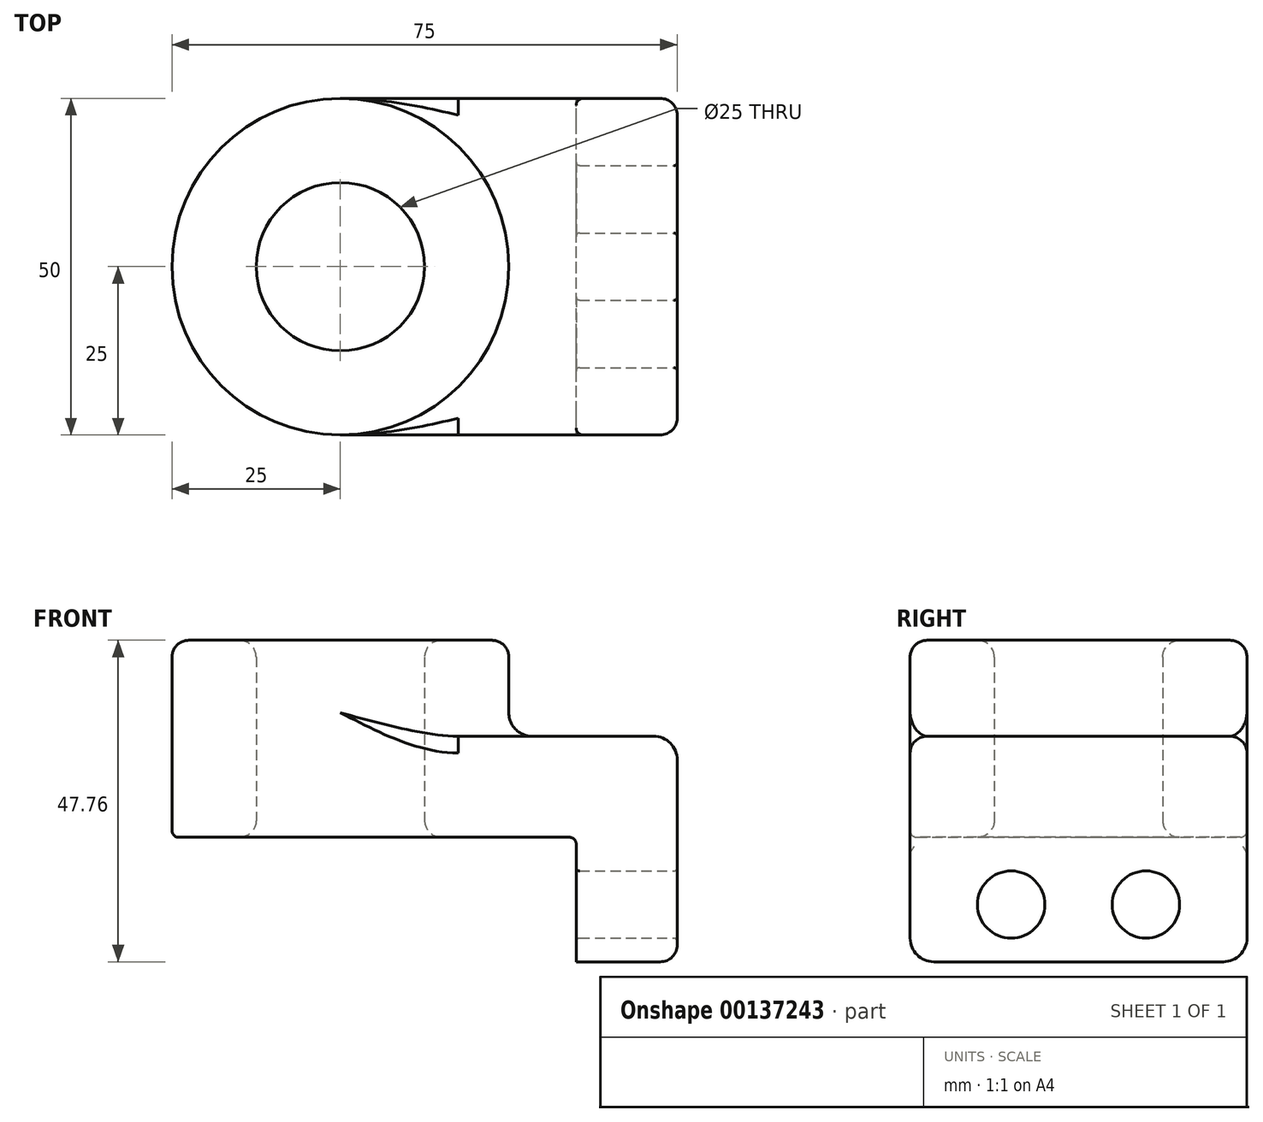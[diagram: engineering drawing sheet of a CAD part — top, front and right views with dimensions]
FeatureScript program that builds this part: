
annotation { "Feature Type Name" : "Feature", "Feature Type Description" : "" }
export const myFeature = defineFeature(function(context is Context, id is Id, definition is map)
    precondition{}
    {
        {
            var Q0;
            Q0=qCreatedBy(makeId("Top.planeOp"),FACE);
            var sketch = newSketch(context, id + "F0", { "sketchPlane" : qUnion([Q0])});
            skLineSegment(sketch, "E0.bottom", {"start": v(25, 25) * mm, "end": v(-25, 25) * mm});
            skLineSegment(sketch, "E0.top", {"start": v(25, -25) * mm, "end": v(-25, -25) * mm});
            skLineSegment(sketch, "E0.left", {"start": v(25, 25) * mm, "end": v(25, -25) * mm});
            skLineSegment(sketch, "E0.right", {"start": v(-25, 25) * mm, "end": v(-25, -25) * mm});
            skPoint(sketch, "E0.middle", {"position": v(0, 0) * mm});
            skCircle(sketch, "E1", {"center": v(-25, 0) * mm, "radius": 25 * mm});
            skCircle(sketch, "E2", {"center": v(-25, 0) * mm, "radius": 12.5 * mm});
            skSolve(sketch);
        }
        {
            var Q0;
            Q0 = qSketchRegion(id + "F0", true);
            extrude(context, id + "F1", {"entities" : qUnion([Q0]), "depth" : 15 * mm});
        }
        {
            var Q0;
            {var subQ1=sQuery(id+"F0.wireOp",EDGE,"E0.right");var subQ3=sQuery(id+"F0.wireOp",EDGE,"E2");var subQ4=makeQuery(id+"F0.imprint","INTERSECT",VERTEX,{"disambiguationData":[OD(0.0)],"derivedFrom":[subQ1,subQ3]});Q0=makeQuery(id+"F0.imprint","IMPRINT",FACE,{"disambiguationData":[TD([[makeQuery(id+"F0.imprint","IMPRINT",EDGE,{"disambiguationData":[TD([[subQ4,-1.0]])],"derivedFrom":subQ3}),-1.0]])]});}
            var Q1;
            {var subQ1=sQuery(id+"F0.wireOp",EDGE,"E0.right");var subQ3=sQuery(id+"F0.wireOp",EDGE,"E2");var subQ4=makeQuery(id+"F0.imprint","INTERSECT",VERTEX,{"disambiguationData":[OD(0.0)],"derivedFrom":[subQ1,subQ3]});Q1=makeQuery(id+"F0.imprint","IMPRINT",FACE,{"disambiguationData":[TD([[makeQuery(id+"F0.imprint","IMPRINT",EDGE,{"disambiguationData":[TD([[subQ4,1.0]])],"derivedFrom":subQ3}),-1.0]])]});}
            extrude(context, id + "F2", {"entities" : qUnion([Q0, Q1]), "operationType" : NewBodyOperationType.ADD, "depth" : 29.26 * mm});
        }
        {
            var Q0;
            Q0=makeQuery(id+"F1.opExtrude","SWEPT_FACE",FACE,{"disambiguationData":[OSD([sQuery(id+"F0.wireOp",EDGE,"E0.left")])]});
            var sketch = newSketch(context, id + "F3", { "sketchPlane" : qUnion([Q0])});
            skLineSegment(sketch, "E3.bottom", {"start": v(-25, 15) * mm, "end": v(25, 15) * mm});
            skLineSegment(sketch, "E3.top", {"start": v(-25, -18.5) * mm, "end": v(25, -18.5) * mm});
            skLineSegment(sketch, "E3.left", {"start": v(-25, 15) * mm, "end": v(-25, -18.5) * mm});
            skLineSegment(sketch, "E3.right", {"start": v(25, 15) * mm, "end": v(25, -18.5) * mm});
            skCircle(sketch, "E4", {"center": v(-10, -10) * mm, "radius": 5 * mm});
            skLineSegment(sketch, "E5", {"start": v(0, 0) * mm, "end": v(0, -18.5) * mm, "construction": true});
            skCircle(sketch, "E6.MirrorC", {"center": v(10, -10) * mm, "radius": 5 * mm});
            skSolve(sketch);
        }
        {
            var Q0;
            Q0 = qSketchRegion(id + "F3", true);
            extrude(context, id + "F4", {"entities" : qUnion([Q0]), "operationType" : NewBodyOperationType.ADD, "oppositeDirection" : true, "depth" : 15 * mm});
        }
        {
            var Q0;
            {var subQ0=sQuery(id+"F0.wireOp",EDGE,"E1");Q0=makeQuery(id+"F2.boolean.opBoolean","INTERSECT",EDGE,{"derivedFrom":[makeQuery(id+"F1.opExtrude","CAP_FACE",FACE,{"disambiguationData":[OSD([sQuery(id+"F0.wireOp",EDGE,"E0.bottom"),sQuery(id+"F0.wireOp",EDGE,"E0.top"),sQuery(id+"F0.wireOp",EDGE,"E0.left"),subQ0,sQuery(id+"F0.wireOp",EDGE,"E2")])],"isStart":false}),makeQuery(id+"F2.opExtrude","SWEPT_FACE",FACE,{"disambiguationData":[OSD([subQ0])]})]});}
            var Q1;
            Q1=makeQuery(id+"F1.opExtrude","CAP_EDGE",EDGE,{"disambiguationData":[OSD([sQuery(id+"F0.wireOp",EDGE,"E0.left")])],"isStart":false});
            var Q2;
            Q2=makeQuery(id+"F4.opExtrude","SWEPT_EDGE",EDGE,{"disambiguationData":[OSD([sQuery(id+"F3.wireOp",EDGE,"E3.top"),sQuery(id+"F3.wireOp",EDGE,"E3.left")])]});
            var Q3;
            Q3=makeQuery(id+"F4.opExtrude","SWEPT_EDGE",EDGE,{"disambiguationData":[OSD([sQuery(id+"F3.wireOp",EDGE,"E3.top"),sQuery(id+"F3.wireOp",EDGE,"E3.right")])]});
            fillet(context, id + "F5", {"entities" : qUnion([Q0, Q1, Q2, Q3]), "radius" : 3.5 * mm, "tangentPropagation" : true, "allowEdgeOverflow" : false});
        }
        {
            var Q0;
            Q0=makeQuery(id+"F1.opExtrude","CAP_EDGE",EDGE,{"disambiguationData":[OSD([sQuery(id+"F0.wireOp",EDGE,"E0.top")])],"isStart":false});
            var Q1;
            {var subQ0=sQuery(id+"F0.wireOp",EDGE,"E2");Q1=makeQuery(id+"F2.boolean.opBoolean","MERGE",FACE,{"derivedFrom":[makeQuery(id+"F1.opExtrude","SWEPT_FACE",FACE,{"disambiguationData":[OSD([subQ0])]}),makeQuery(id+"F2.opExtrude","SWEPT_FACE",FACE,{"disambiguationData":[OSD([subQ0])]})]});}
            var Q2;
            Q2=makeQuery(id+"F2.opExtrude","CAP_EDGE",EDGE,{"disambiguationData":[OSD([sQuery(id+"F0.wireOp",EDGE,"E1")])],"isStart":false});
            fillet(context, id + "F6", {"entities" : qUnion([Q0, Q1, Q2]), "radius" : 2.5 * mm, "tangentPropagation" : true, "allowEdgeOverflow" : false});
        }
        {
            var Q0;
            Q0=makeQuery(id+"F1.opExtrude","CAP_EDGE",EDGE,{"disambiguationData":[OSD([sQuery(id+"F0.wireOp",EDGE,"E0.top")])],"isStart":true});
            var Q1;
            Q1=makeQuery(id+"F4.boolean.opBoolean","INTERSECT",EDGE,{"derivedFrom":[makeQuery(id+"F1.opExtrude","CAP_FACE",FACE,{"disambiguationData":[OSD([sQuery(id+"F0.wireOp",EDGE,"E0.bottom"),sQuery(id+"F0.wireOp",EDGE,"E0.top"),sQuery(id+"F0.wireOp",EDGE,"E0.left"),sQuery(id+"F0.wireOp",EDGE,"E1"),sQuery(id+"F0.wireOp",EDGE,"E2")])],"isStart":true}),makeQuery(id+"F4.opExtrude","CAP_FACE",FACE,{"disambiguationData":[OSD([sQuery(id+"F3.wireOp",EDGE,"E3.bottom"),sQuery(id+"F3.wireOp",EDGE,"E3.top"),sQuery(id+"F3.wireOp",EDGE,"E3.left"),sQuery(id+"F3.wireOp",EDGE,"E4"),sQuery(id+"F3.wireOp",EDGE,"E3.right"),sQuery(id+"F3.wireOp",EDGE,"E6.MirrorC")])],"isStart":false})]});
            fillet(context, id + "F7", {"entities" : qUnion([Q0, Q1]), "radius" : 1 * mm, "tangentPropagation" : true, "allowEdgeOverflow" : false});
        }
        {
            var Q0;
            Q0=makeQuery(id+"F4.opExtrude","SWEPT_FACE",FACE,{"disambiguationData":[OSD([sQuery(id+"F3.wireOp",EDGE,"E4")])]});
            var Q1;
            Q1=makeQuery(id+"F4.opExtrude","SWEPT_FACE",FACE,{"disambiguationData":[OSD([sQuery(id+"F3.wireOp",EDGE,"E6.MirrorC")])]});
            fillet(context, id + "F8", {"entities" : qUnion([Q0, Q1]), "radius" : 0.5 * mm, "tangentPropagation" : true, "allowEdgeOverflow" : false});
        }
    });
